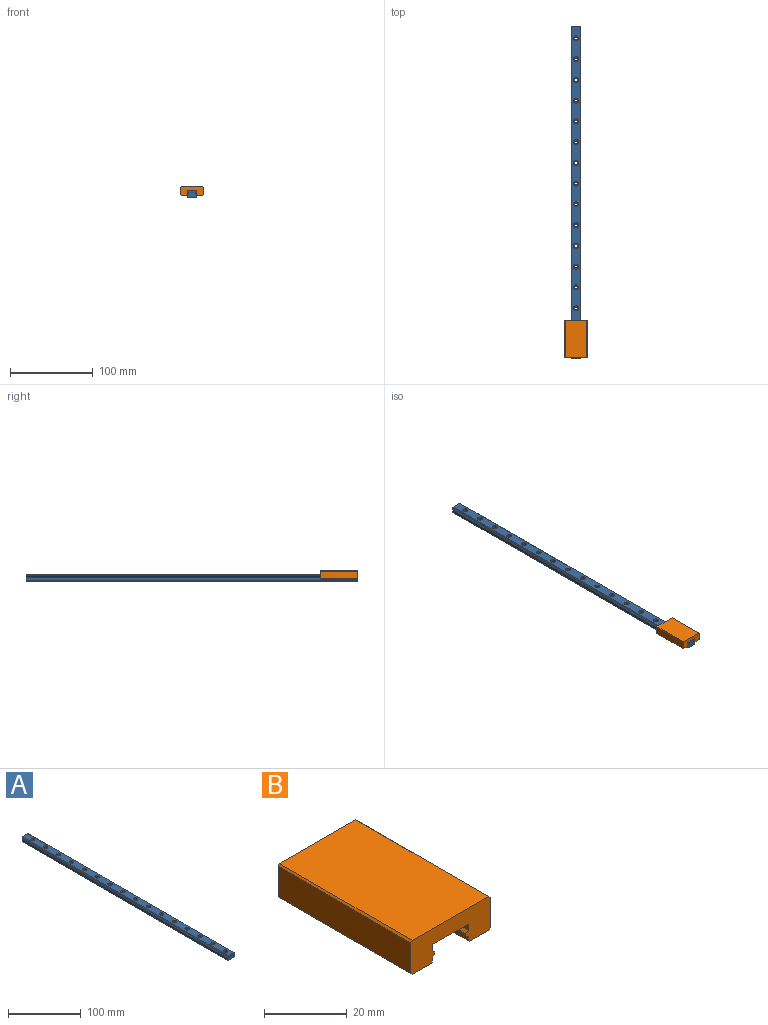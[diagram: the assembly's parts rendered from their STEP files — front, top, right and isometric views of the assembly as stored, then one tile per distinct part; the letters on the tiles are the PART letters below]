
ASSEMBLY  parts=2 mates=1
PART A: 70 faces, bbox 12x400x8 mm
  f0: plane 400x0.5mm, normal (0,0,-1), area 200mm2, adj f1,f15,f16,f17
  f1: plane 400x0.5mm, normal (-1,0,0), area 200mm2, adj f0,f2,f16,f17
  f2: plane 400x0.5mm, normal (0,0,1), area 200mm2, adj f1,f3,f16,f17
  f3: plane 400x1mm, normal (-0.71,0,0.71), area 565.7mm2, adj f2,f4,f16,f17
  f4: plane 400x3.5mm, normal (-1,0,0), area 1400mm2, adj f3,f16,f17,f18
  f5: plane 400x11mm, normal (0,0,-1), area 4246.1mm2, adj f16,f17,f18,f19,f22,f25,f28,f31
  f6: plane 400x3.5mm, normal (1,0,0), area 1400mm2, adj f7,f16,f17,f19
  f7: plane 400x1mm, normal (0.71,0,0.71), area 565.7mm2, adj f6,f8,f16,f17
  f8: plane 400x0.5mm, normal (0,0,1), area 200mm2, adj f7,f9,f16,f17
  f9: plane 400x0.5mm, normal (1,0,0), area 200mm2, adj f8,f10,f16,f17
  f10: plane 400x0.5mm, normal (0,0,-1), area 200mm2, adj f9,f11,f16,f17
  f11: plane 400x1mm, normal (0.71,0,-0.71), area 565.7mm2, adj f10,f12,f16,f17
  f12: plane 400x1mm, normal (1,0,0), area 400mm2, adj f11,f16,f17,f21
  f13: plane 400x11mm, normal (0,0,1), area 3947.6mm2, adj f16,f17,f20,f21,f24,f27,f30,f33
  f14: plane 400x1mm, normal (-1,0,0), area 400mm2, adj f15,f16,f17,f20
  f15: plane 400x1mm, normal (-0.71,0,-0.71), area 565.7mm2, adj f0,f14,f16,f17
  f16: plane 12x8mm, normal (0,-1,0), area 92mm2, adj f0,f1,f2,f3,f4,f5,f6,f7
  f17: plane 12x8mm, normal (0,1,0), area 92mm2, adj f0,f1,f2,f3,f4,f5,f6,f7
  f18: plane 400x0.5mm, normal (-0.71,0,-0.71), area 282.8mm2, adj f4,f5,f16,f17
  f19: plane 400x0.5mm, normal (0.71,0,-0.71), area 282.8mm2, adj f5,f6,f16,f17
  f20: plane 400x0.5mm, normal (-0.71,0,0.71), area 282.8mm2, adj f13,f14,f16,f17
  f21: plane 400x0.5mm, normal (0.71,0,0.71), area 282.8mm2, adj f12,f13,f16,f17
  f22: cylinder r=1.75mm len=3.5mm, axis (0,0,1), area 38.5mm2, adj f5,f23
  f23: plane 6x6mm, normal (0,0,1), area 18.7mm2, adj f22,f24
  f24: cylinder r=3mm len=6mm, axis (0,0,1), area 84.8mm2, adj f13,f23
  f25: cylinder r=1.75mm len=3.5mm, axis (0,0,1), area 38.5mm2, adj f5,f26
  f26: plane 6x6mm, normal (0,0,1), area 18.7mm2, adj f25,f27
  f27: cylinder r=3mm len=6mm, axis (0,0,1), area 84.8mm2, adj f13,f26
  f28: cylinder r=1.75mm len=3.5mm, axis (0,0,1), area 38.5mm2, adj f5,f29
  f29: plane 6x6mm, normal (0,0,1), area 18.7mm2, adj f28,f30
  f30: cylinder r=3mm len=6mm, axis (0,0,1), area 84.8mm2, adj f13,f29
  f31: cylinder r=1.75mm len=3.5mm, axis (0,0,1), area 38.5mm2, adj f5,f32
  f32: plane 6x6mm, normal (0,0,1), area 18.7mm2, adj f31,f33
  f33: cylinder r=3mm len=6mm, axis (0,0,1), area 84.8mm2, adj f13,f32
  f34: cylinder r=1.75mm len=3.5mm, axis (0,0,1), area 38.5mm2, adj f5,f35
  f35: plane 6x6mm, normal (0,0,1), area 18.7mm2, adj f34,f36
  f36: cylinder r=3mm len=6mm, axis (0,0,1), area 84.8mm2, adj f13,f35
  f37: cylinder r=1.75mm len=3.5mm, axis (0,0,1), area 38.5mm2, adj f5,f38
  f38: plane 6x6mm, normal (0,0,1), area 18.7mm2, adj f37,f39
  f39: cylinder r=3mm len=6mm, axis (0,0,1), area 84.8mm2, adj f13,f38
  f40: cylinder r=1.75mm len=3.5mm, axis (0,0,1), area 38.5mm2, adj f5,f41
  f41: plane 6x6mm, normal (0,0,1), area 18.7mm2, adj f40,f42
  f42: cylinder r=3mm len=6mm, axis (0,0,1), area 84.8mm2, adj f13,f41
  f43: cylinder r=1.75mm len=3.5mm, axis (0,0,1), area 38.5mm2, adj f5,f44
  f44: plane 6x6mm, normal (0,0,1), area 18.7mm2, adj f43,f45
  f45: cylinder r=3mm len=6mm, axis (0,0,1), area 84.8mm2, adj f13,f44
  f46: cylinder r=1.75mm len=3.5mm, axis (0,0,1), area 38.5mm2, adj f5,f47
  f47: plane 6x6mm, normal (0,0,1), area 18.7mm2, adj f46,f48
  f48: cylinder r=3mm len=6mm, axis (0,0,1), area 84.8mm2, adj f13,f47
  f49: cylinder r=1.75mm len=3.5mm, axis (0,0,1), area 38.5mm2, adj f5,f50
  f50: plane 6x6mm, normal (0,0,1), area 18.7mm2, adj f49,f51
  f51: cylinder r=3mm len=6mm, axis (0,0,1), area 84.8mm2, adj f13,f50
  f52: cylinder r=1.75mm len=3.5mm, axis (0,0,1), area 38.5mm2, adj f5,f53
  f53: plane 6x6mm, normal (0,0,1), area 18.7mm2, adj f52,f54
  f54: cylinder r=3mm len=6mm, axis (0,0,1), area 84.8mm2, adj f13,f53
  f55: cylinder r=1.75mm len=3.5mm, axis (0,0,1), area 38.5mm2, adj f5,f56
  f56: plane 6x6mm, normal (0,0,1), area 18.7mm2, adj f55,f57
  f57: cylinder r=3mm len=6mm, axis (0,0,1), area 84.8mm2, adj f13,f56
  f58: cylinder r=1.75mm len=3.5mm, axis (0,0,1), area 38.5mm2, adj f5,f59
  f59: plane 6x6mm, normal (0,0,1), area 18.7mm2, adj f58,f60
  f60: cylinder r=3mm len=6mm, axis (0,0,1), area 84.8mm2, adj f13,f59
  f61: cylinder r=1.75mm len=3.5mm, axis (0,0,1), area 38.5mm2, adj f5,f62
  f62: plane 6x6mm, normal (0,0,1), area 18.7mm2, adj f61,f63
  f63: cylinder r=3mm len=6mm, axis (0,0,1), area 84.8mm2, adj f13,f62
  f64: cylinder r=1.75mm len=3.5mm, axis (0,0,1), area 38.5mm2, adj f5,f65
  f65: plane 6x6mm, normal (0,0,1), area 18.7mm2, adj f64,f66
  f66: cylinder r=3mm len=6mm, axis (0,0,1), area 84.8mm2, adj f13,f65
  f67: cylinder r=1.75mm len=3.5mm, axis (0,0,1), area 38.5mm2, adj f5,f68
  f68: plane 6x6mm, normal (0,0,1), area 18.7mm2, adj f67,f69
  f69: cylinder r=3mm len=6mm, axis (0,0,1), area 84.8mm2, adj f13,f68
PART B: 24 faces, bbox 27x45.4x10 mm
  f0: plane 45.4x0.5mm, normal (1,0,0), area 22.7mm2, adj f1,f15,f16,f17
  f1: plane 45.4x0.7mm, normal (0.71,0,0.71), area 44.9mm2, adj f0,f2,f16,f17
  f2: plane 45.4x1.82mm, normal (1,0,0), area 82.5mm2, adj f1,f3,f16,f17
  f3: plane 45.4x12mm, normal (0,0,-1), area 544.8mm2, adj f2,f4,f16,f17
  f4: plane 45.4x1.82mm, normal (-1,0,0), area 82.5mm2, adj f3,f5,f16,f17
  f5: plane 45.4x0.7mm, normal (-0.71,0,0.71), area 44.9mm2, adj f4,f6,f16,f17
  f6: plane 45.4x0.5mm, normal (-1,0,0), area 22.7mm2, adj f5,f7,f16,f17
  f7: plane 45.4x0.7mm, normal (-0.71,0,-0.71), area 44.9mm2, adj f6,f8,f16,f17
  f8: plane 45.4x1.09mm, normal (-1,0,0), area 49.7mm2, adj f7,f16,f17,f18
  f9: plane 45.4x6.5mm, normal (0,0,-1), area 295.1mm2, adj f16,f17,f18,f23
  f10: plane 45.4x9mm, normal (1,0,0), area 408.6mm2, adj f16,f17,f22,f23
  f11: plane 45.4x26mm, normal (0,0,1), area 1180.4mm2, adj f16,f17,f21,f22
  f12: plane 45.4x9mm, normal (-1,0,0), area 408.6mm2, adj f16,f17,f20,f21
  f13: plane 45.4x6.5mm, normal (0,0,-1), area 295.1mm2, adj f16,f17,f19,f20
  f14: plane 45.4x1.09mm, normal (1,0,0), area 49.7mm2, adj f15,f16,f17,f19
  f15: plane 45.4x0.7mm, normal (0.71,0,-0.71), area 44.9mm2, adj f0,f14,f16,f17
  f16: plane 27x10mm, normal (0,-1,0), area 207.2mm2, adj f0,f1,f2,f3,f4,f5,f6,f7
  f17: plane 27x10mm, normal (0,1,0), area 207.2mm2, adj f0,f1,f2,f3,f4,f5,f6,f7
  f18: plane 45.4x0.5mm, normal (-0.71,0,-0.71), area 32.1mm2, adj f8,f9,f16,f17
  f19: plane 45.4x0.5mm, normal (0.71,0,-0.71), area 32.1mm2, adj f13,f14,f16,f17
  f20: plane 45.4x0.5mm, normal (-0.71,0,-0.71), area 32.1mm2, adj f12,f13,f16,f17
  f21: plane 45.4x0.5mm, normal (-0.71,0,0.71), area 32.1mm2, adj f11,f12,f16,f17
  f22: plane 45.4x0.5mm, normal (0.71,0,0.71), area 32.1mm2, adj f10,f11,f16,f17
  f23: plane 45.4x0.5mm, normal (0.71,0,-0.71), area 32.1mm2, adj f9,f10,f16,f17
PLACE A t=(0,15,0)mm
PLACE B t=(0,-339.6,0)mm
MATE slider A.f17 <-> B.f17  axis (0,1,0) through (0,15,8)mm
